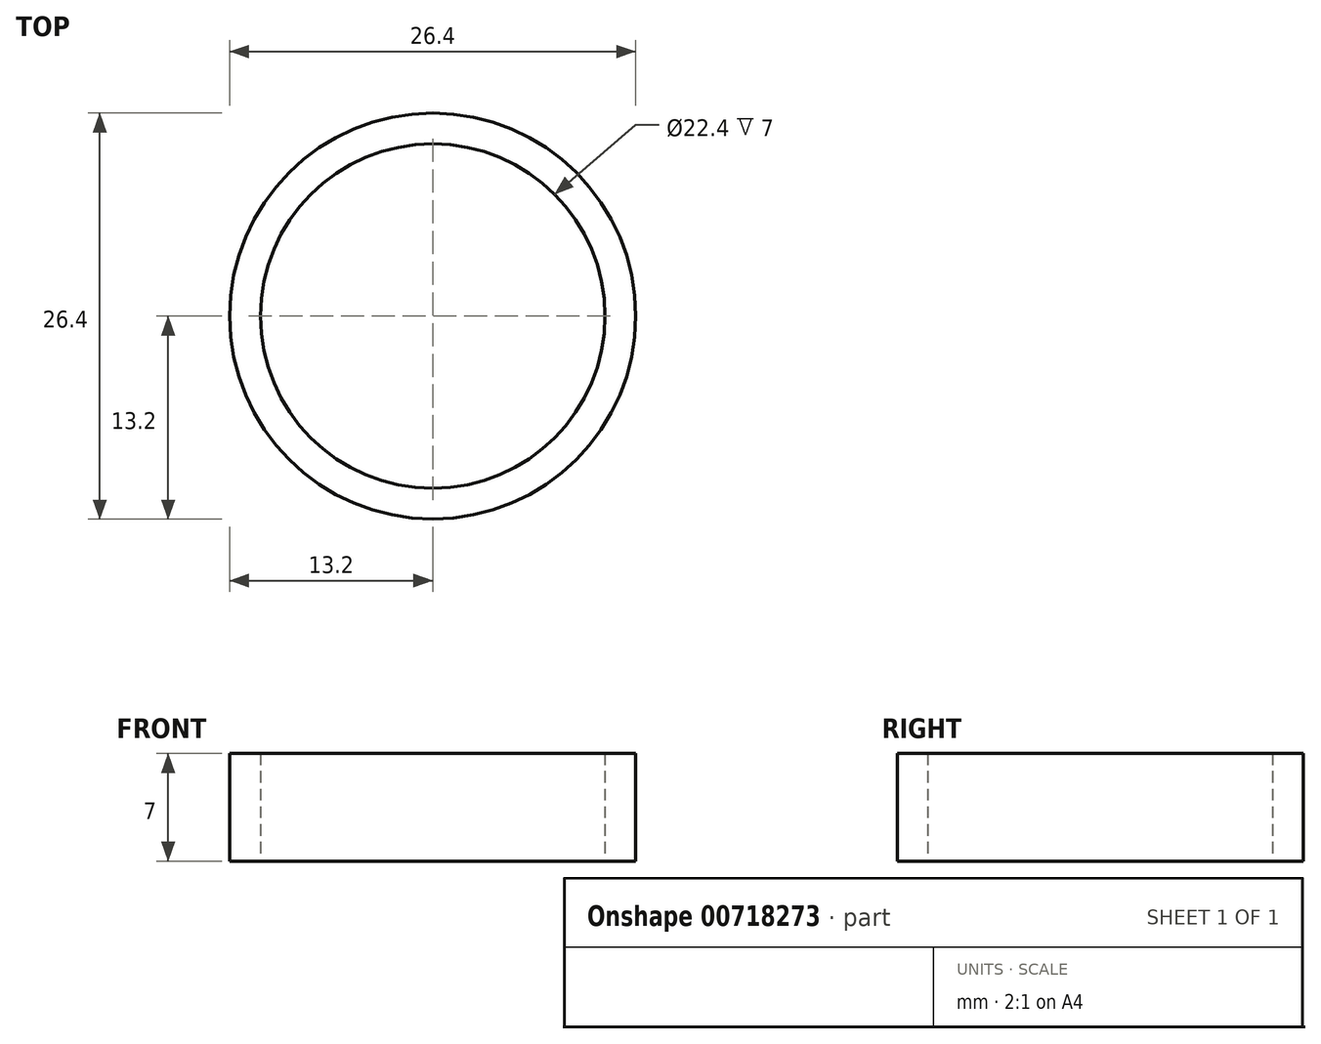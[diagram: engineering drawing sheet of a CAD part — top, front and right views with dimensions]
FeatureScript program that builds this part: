
annotation { "Feature Type Name" : "Feature", "Feature Type Description" : "" }
export const myFeature = defineFeature(function(context is Context, id is Id, definition is map)
    precondition{}
    {
        {
            var Q0;
            Q0=qCreatedBy(makeId("Top.planeOp"),FACE);
            var sketch = newSketch(context, id + "F0", { "sketchPlane" : qUnion([Q0])});
            skCircle(sketch, "E0", {"center": v(0, 0) * mm, "radius": 13.2 * mm});
            skCircle(sketch, "E1", {"center": v(0, 0) * mm, "radius": 11.2 * mm});
            skSolve(sketch);
        }
        {
            var Q0;
            Q0=makeQuery(id+"F0.imprint","IMPRINT",FACE,{"disambiguationData":[TD([[makeQuery(id+"F0.imprint","IMPRINT",EDGE,{"derivedFrom":sQuery(id+"F0.wireOp",EDGE,"E0")}),1.0]])]});
            extrude(context, id + "F1", {"entities" : qUnion([Q0]), "depth" : 7 * mm, "offsetDistance" : 25 * mm});
        }
    });
